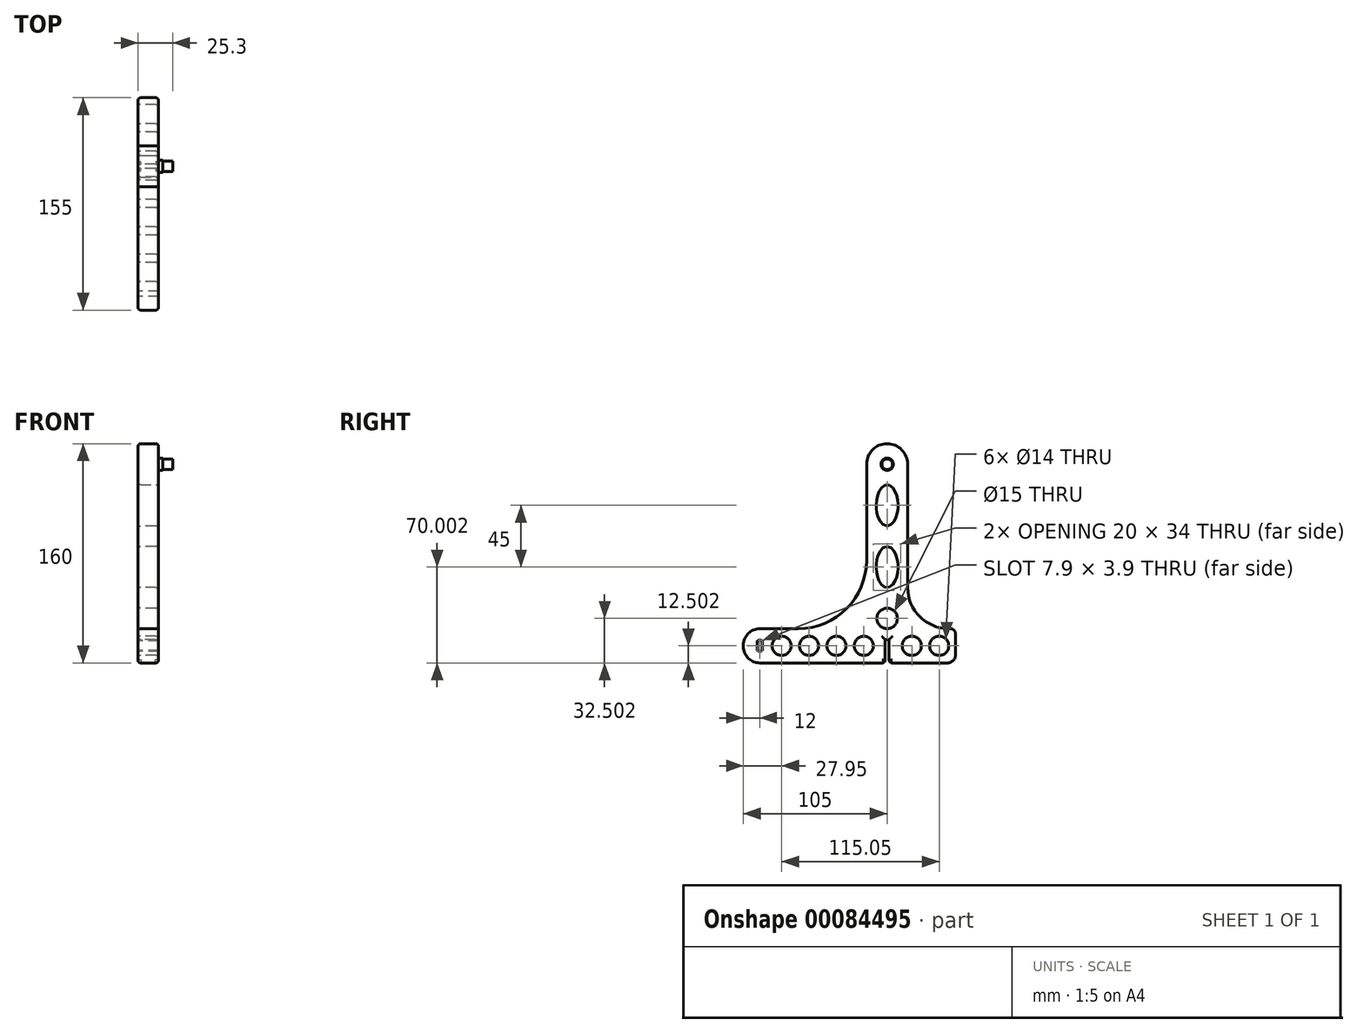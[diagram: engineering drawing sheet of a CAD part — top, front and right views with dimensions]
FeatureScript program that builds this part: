
annotation { "Feature Type Name" : "Feature", "Feature Type Description" : "" }
export const myFeature = defineFeature(function(context is Context, id is Id, definition is map)
    precondition{}
    {
        {
            var Q0;
            Q0=qCreatedBy(makeId("Right.planeOp"),FACE);
            var sketch = newSketch(context, id + "F0", { "sketchPlane" : qUnion([Q0])});
            skArc(sketch, "E0", {"start": v(15, 65.9) * mm, "mid": v(0, 80.9) * mm, "end": v(-15, 65.9) * mm});
            skLineSegment(sketch, "E1.bottom", {"start": v(-15, 65.9) * mm, "end": v(15, 65.9) * mm, "construction": true});
            skLineSegment(sketch, "E1.top", {"start": v(-15, -79.1) * mm, "end": v(-1.45, -79.1) * mm});
            skLineSegment(sketch, "E1.left", {"start": v(-15, 65.9) * mm, "end": v(-15, -4.1) * mm});
            skLineSegment(sketch, "E1.right", {"start": v(15, 65.9) * mm, "end": v(15, -24.1) * mm});
            skLineSegment(sketch, "E2.bottom", {"start": v(15, -79.1) * mm, "end": v(44, -79.1) * mm});
            skLineSegment(sketch, "E2.top", {"start": v(45, -54.1) * mm, "end": v(46, -54.1) * mm});
            skLineSegment(sketch, "E2.left", {"start": v(15, -79.1) * mm, "end": v(15, -54.1) * mm, "construction": true});
            skLineSegment(sketch, "E2.right", {"start": v(50, -73.1) * mm, "end": v(50, -58.1) * mm});
            skPoint(sketch, "E3.newPointA", {"position": v(15, -54.1) * mm});
            skPoint(sketch, "E3.newPointB", {"position": v(15, -54.1) * mm});
            skArc(sketch, "E3.filletArc", {"start": v(15, -24.1) * mm, "mid": v(23.79, -45.31) * mm, "end": v(45, -54.1) * mm});
            skPoint(sketch, "E4.visualSharp", {"position": v(50, -54.1) * mm});
            skArc(sketch, "E4.filletArc", {"start": v(50, -58.1) * mm, "mid": v(48.83, -55.27) * mm, "end": v(46, -54.1) * mm});
            skPoint(sketch, "E5.visualSharp", {"position": v(50, -79.1) * mm});
            skArc(sketch, "E5.filletArc", {"start": v(44, -79.1) * mm, "mid": v(48.24, -77.34) * mm, "end": v(50, -73.1) * mm});
            skLineSegment(sketch, "E6", {"start": v(50, -54.1) * mm, "end": v(50, -79.1) * mm, "construction": true});
            skLineSegment(sketch, "E7.bottom", {"start": v(-15, -79.1) * mm, "end": v(-93, -79.1) * mm});
            skLineSegment(sketch, "E7.top", {"start": v(-65, -54.1) * mm, "end": v(-93, -54.1) * mm});
            skLineSegment(sketch, "E7.right", {"start": v(-105, -67.1) * mm, "end": v(-105, -66.1) * mm});
            skArc(sketch, "E8.filletArc", {"start": v(-65, -54.1) * mm, "mid": v(-29.64, -39.45) * mm, "end": v(-15, -4.1) * mm});
            skPoint(sketch, "E9.visualSharp", {"position": v(-105, -54.1) * mm});
            skArc(sketch, "E9.filletArc", {"start": v(-93, -54.1) * mm, "mid": v(-101.49, -57.61) * mm, "end": v(-105, -66.1) * mm});
            skPoint(sketch, "E10.visualSharp", {"position": v(-105, -79.1) * mm});
            skArc(sketch, "E10.filletArc", {"start": v(-105, -67.1) * mm, "mid": v(-101.49, -75.58) * mm, "end": v(-93, -79.1) * mm});
            skLineSegment(sketch, "E11", {"start": v(45, -54.1) * mm, "end": v(-65, -54.1) * mm, "construction": true});
            skLineSegment(sketch, "E12", {"start": v(0, 65.9) * mm, "end": v(0, -54.1) * mm, "construction": true});
            skPoint(sketch, "E13", {"position": v(0, 5.9) * mm});
            skLineSegment(sketch, "E14", {"start": v(0, 5.9) * mm, "end": v(0, 65.9) * mm, "construction": true});
            skPoint(sketch, "E15", {"position": v(0, 35.9) * mm});
            skLineSegment(sketch, "E16", {"start": v(0, 5.9) * mm, "end": v(0, -54.1) * mm, "construction": true});
            skPoint(sketch, "E17", {"position": v(0, -24.1) * mm});
            skLineSegment(sketch, "E18", {"start": v(50, -66.6) * mm, "end": v(-105, -66.6) * mm, "construction": true});
            skLineSegment(sketch, "E19", {"start": v(0, 65.9) * mm, "end": v(0, 35.9) * mm, "construction": true});
            skLineSegment(sketch, "E20", {"start": v(0, 35.9) * mm, "end": v(0, 5.9) * mm, "construction": true});
            skLineSegment(sketch, "E21", {"start": v(0, 5.9) * mm, "end": v(0, -24.1) * mm, "construction": true});
            skLineSegment(sketch, "E22", {"start": v(0, -24.1) * mm, "end": v(0, -54.1) * mm, "construction": true});
            skPoint(sketch, "E23", {"position": v(0, 50.9) * mm});
            skPoint(sketch, "E24", {"position": v(0, 20.9) * mm});
            skPoint(sketch, "E25", {"position": v(0, -9.1) * mm});
            skPoint(sketch, "E26", {"position": v(0, -39.1) * mm});
            skEllipse(sketch, "E27", {"center": v(0, 35.9) * mm, "majorRadius": 15 * mm, "minorRadius": 8 * mm, "majorAxis": v(0, -1)});
            skLineSegment(sketch, "E28", {"start": v(8, 65.9) * mm, "end": v(8, -54.1) * mm, "construction": true});
            skEllipse(sketch, "E29", {"center": v(0, -9.1) * mm, "majorRadius": 15 * mm, "minorRadius": 8 * mm, "majorAxis": v(0, 1)});
            skPoint(sketch, "E30", {"position": v(0, -46.6) * mm});
            skCircle(sketch, "E31", {"center": v(0, -46.6) * mm, "radius": 7.5 * mm});
            skPoint(sketch, "E32", {"position": v(-93, -66.6) * mm});
            skLineSegment(sketch, "E33.bottom", {"start": v(1.45, -62.1) * mm, "end": v(-1.45, -62.1) * mm});
            skLineSegment(sketch, "E33.left", {"start": v(1.45, -62.1) * mm, "end": v(1.45, -79.1) * mm});
            skLineSegment(sketch, "E33.right", {"start": v(-1.45, -62.1) * mm, "end": v(-1.45, -79.1) * mm});
            skPoint(sketch, "E33.middle", {"position": v(0, -79.1) * mm});
            skPoint(sketch, "E33.top.end.orphan", {"position": v(-1.45, -96.1) * mm});
            skPoint(sketch, "E33.top.start.orphan", {"position": v(1.45, -96.1) * mm});
            skLineSegment(sketch, "E34.trimOffspring", {"start": v(1.45, -79.1) * mm, "end": v(15, -79.1) * mm});
            skCircle(sketch, "E35", {"center": v(0, 65.9) * mm, "radius": 4.5 * mm});
            skCircle(sketch, "E36", {"center": v(0, 65.9) * mm, "radius": 3.9 * mm});
            skCircle(sketch, "E37", {"center": v(-93, -66.6) * mm, "radius": 3.95 * mm});
            skLineSegment(sketch, "E38", {"start": v(-89.05, -54.1) * mm, "end": v(-89.05, -79.1) * mm, "construction": true});
            skLineSegment(sketch, "E39", {"start": v(-96.95, -54.77) * mm, "end": v(-96.95, -78.43) * mm, "construction": true});
            skLineSegment(sketch, "E40", {"start": v(-91.05, -63.16) * mm, "end": v(-91.05, -70.03) * mm});
            skLineSegment(sketch, "E41", {"start": v(-94.95, -63.16) * mm, "end": v(-94.95, -70.03) * mm});
            skLineSegment(sketch, "E42", {"start": v(-96.95, -66.6) * mm, "end": v(-94.95, -66.6) * mm, "construction": true});
            skPoint(sketch, "E43.orphan", {"position": v(-94.95, -54.26) * mm});
            skPoint(sketch, "E44.orphan", {"position": v(-94.95, -78.94) * mm});
            skLineSegment(sketch, "E45", {"start": v(-91.05, -66.6) * mm, "end": v(-89.05, -66.6) * mm, "construction": true});
            skLineSegment(sketch, "E46", {"start": v(-94.95, -66.6) * mm, "end": v(-96.95, -66.6) * mm, "construction": true});
            skCircle(sketch, "E47", {"center": v(-77.05, -66.6) * mm, "radius": 7 * mm});
            skCircle(sketch, "E48.1.0.0", {"center": v(-57.05, -66.6) * mm, "radius": 7 * mm});
            skCircle(sketch, "E48.2.0.0", {"center": v(-37.05, -66.6) * mm, "radius": 7 * mm});
            skLineSegment(sketch, "E48.direction1", {"start": v(-77.05, -66.6) * mm, "end": v(-57.05, -66.6) * mm, "construction": true});
            skCircle(sketch, "E49", {"center": v(38, -66.6) * mm, "radius": 7 * mm});
            skCircle(sketch, "E50.1.0.0", {"center": v(18, -66.6) * mm, "radius": 7 * mm});
            skLineSegment(sketch, "E50.1.0.1", {"start": v(-5, -79.1) * mm, "end": v(24, -79.1) * mm});
            skLineSegment(sketch, "E50.direction1", {"start": v(38, -66.6) * mm, "end": v(18, -66.6) * mm, "construction": true});
            skCircle(sketch, "E51.0.3.0", {"center": v(-17.05, -66.6) * mm, "radius": 7 * mm});
            skSolve(sketch);
        }
        {
            var Q0;
            Q0=makeQuery(id+"F0.imprint","IMPRINT",FACE,{"disambiguationData":[TD([[makeQuery(id+"F0.imprint","IMPRINT",EDGE,{"derivedFrom":sQuery(id+"F0.wireOp",EDGE,"E0")}),1.0]])]});
            var Q1;
            {var subQ0=sQuery(id+"F0.wireOp",EDGE,"E40");Q1=makeQuery(id+"F0.imprint","IMPRINT",FACE,{"disambiguationData":[TD([[makeQuery(id+"F0.imprint","IMPRINT",EDGE,{"derivedFrom":subQ0}),1.0]])]});}
            var Q2;
            {var subQ0=sQuery(id+"F0.wireOp",EDGE,"E41");Q2=makeQuery(id+"F0.imprint","IMPRINT",FACE,{"disambiguationData":[TD([[makeQuery(id+"F0.imprint","IMPRINT",EDGE,{"derivedFrom":subQ0}),-1.0]])]});}
            extrude(context, id + "F1", {"entities" : qUnion([Q0, Q1, Q2]), "depth" : 15 * mm});
        }
        {
            var Q0;
            Q0=makeQuery(id+"F0.imprint","IMPRINT",FACE,{"disambiguationData":[TD([[makeQuery(id+"F0.imprint","IMPRINT",EDGE,{"derivedFrom":sQuery(id+"F0.wireOp",EDGE,"E35")}),1.0]])]});
            extrude(context, id + "F2", {"entities" : qUnion([Q0]), "operationType" : NewBodyOperationType.ADD, "depth" : 18 * mm});
        }
        {
            var Q0;
            Q0=makeQuery(id+"F0.imprint","IMPRINT",FACE,{"disambiguationData":[TD([[makeQuery(id+"F0.imprint","IMPRINT",EDGE,{"derivedFrom":sQuery(id+"F0.wireOp",EDGE,"E36")}),1.0]])]});
            extrude(context, id + "F3", {"entities" : qUnion([Q0]), "operationType" : NewBodyOperationType.ADD, "depth" : 25.3 * mm});
        }
        {
            var Q0;
            Q0=makeQuery(id+"F1.opExtrude","CAP_EDGE",EDGE,{"disambiguationData":[OSD([sQuery(id+"F0.wireOp",EDGE,"E1.right")])],"isStart":false});
            var Q1;
            Q1=makeQuery(id+"F1.opExtrude","CAP_EDGE",EDGE,{"disambiguationData":[OSD([sQuery(id+"F0.wireOp",EDGE,"E1.right")])],"isStart":true});
            var Q2;
            Q2=makeQuery(id+"F1.opExtrude","CAP_EDGE",EDGE,{"disambiguationData":[OSD([sQuery(id+"F0.wireOp",EDGE,"E27")])],"isStart":false});
            var Q3;
            Q3=makeQuery(id+"F1.opExtrude","CAP_EDGE",EDGE,{"disambiguationData":[OSD([sQuery(id+"F0.wireOp",EDGE,"E27")])],"isStart":true});
            var Q4;
            Q4=makeQuery(id+"F1.opExtrude","CAP_EDGE",EDGE,{"disambiguationData":[OSD([sQuery(id+"F0.wireOp",EDGE,"E29")])],"isStart":true});
            var Q5;
            Q5=makeQuery(id+"F1.opExtrude","CAP_EDGE",EDGE,{"disambiguationData":[OSD([sQuery(id+"F0.wireOp",EDGE,"E29")])],"isStart":false});
            var Q6;
            Q6=makeQuery(id+"F1.opExtrude","CAP_EDGE",EDGE,{"disambiguationData":[OSD([sQuery(id+"F0.wireOp",EDGE,"E31")])],"isStart":true});
            var Q7;
            Q7=makeQuery(id+"F1.opExtrude","CAP_EDGE",EDGE,{"disambiguationData":[OSD([sQuery(id+"F0.wireOp",EDGE,"E31")])],"isStart":false});
            var Q8;
            Q8=makeQuery(id+"F1.opExtrude","CAP_EDGE",EDGE,{"disambiguationData":[OSD([sQuery(id+"F0.wireOp",EDGE,"E35")])],"isStart":false});
            var Q9;
            Q9=makeQuery(id+"F1.opExtrude","CAP_EDGE",EDGE,{"disambiguationData":[OSD([sQuery(id+"F0.wireOp",EDGE,"E47")])],"isStart":false});
            var Q10;
            Q10=makeQuery(id+"F1.opExtrude","CAP_EDGE",EDGE,{"disambiguationData":[OSD([sQuery(id+"F0.wireOp",EDGE,"E48.1.0.0")])],"isStart":false});
            var Q11;
            Q11=makeQuery(id+"F1.opExtrude","CAP_EDGE",EDGE,{"disambiguationData":[OSD([sQuery(id+"F0.wireOp",EDGE,"E48.2.0.0")])],"isStart":false});
            var Q12;
            Q12=makeQuery(id+"F1.opExtrude","CAP_EDGE",EDGE,{"disambiguationData":[OSD([sQuery(id+"F0.wireOp",EDGE,"E48.2.0.0")])],"isStart":true});
            var Q13;
            Q13=makeQuery(id+"F1.opExtrude","CAP_EDGE",EDGE,{"disambiguationData":[OSD([sQuery(id+"F0.wireOp",EDGE,"E48.1.0.0")])],"isStart":true});
            var Q14;
            Q14=makeQuery(id+"F1.opExtrude","CAP_EDGE",EDGE,{"disambiguationData":[OSD([sQuery(id+"F0.wireOp",EDGE,"E47")])],"isStart":true});
            var Q15;
            Q15=makeQuery(id+"F1.opExtrude","CAP_EDGE",EDGE,{"disambiguationData":[OSD([sQuery(id+"F0.wireOp",EDGE,"E51.0.3.0")])],"isStart":false});
            var Q16;
            Q16=makeQuery(id+"F1.opExtrude","CAP_EDGE",EDGE,{"disambiguationData":[OSD([sQuery(id+"F0.wireOp",EDGE,"E50.1.0.0")])],"isStart":false});
            var Q17;
            Q17=makeQuery(id+"F1.opExtrude","CAP_EDGE",EDGE,{"disambiguationData":[OSD([sQuery(id+"F0.wireOp",EDGE,"E49")])],"isStart":false});
            var Q18;
            Q18=makeQuery(id+"F1.opExtrude","CAP_EDGE",EDGE,{"disambiguationData":[OSD([sQuery(id+"F0.wireOp",EDGE,"E51.0.3.0")])],"isStart":true});
            var Q19;
            Q19=makeQuery(id+"F1.opExtrude","CAP_EDGE",EDGE,{"disambiguationData":[OSD([sQuery(id+"F0.wireOp",EDGE,"E50.1.0.0")])],"isStart":true});
            var Q20;
            Q20=makeQuery(id+"F1.opExtrude","CAP_EDGE",EDGE,{"disambiguationData":[OSD([sQuery(id+"F0.wireOp",EDGE,"E49")])],"isStart":true});
            fillet(context, id + "F4", {"entities" : qUnion([Q0, Q1, Q2, Q3, Q4, Q5, Q6, Q7, Q8, Q9, Q10, Q11, Q12, Q13, Q14, Q15, Q16, Q17, Q18, Q19, Q20]), "radius" : 2 * mm, "tangentPropagation" : true, "allowEdgeOverflow" : false});
        }
        {
            var Q0;
            Q0=makeQuery(id+"F1.opExtrude","CAP_EDGE",EDGE,{"disambiguationData":[OSD([sQuery(id+"F0.wireOp",EDGE,"E33.right")])],"isStart":false});
            var Q1;
            Q1=makeQuery(id+"F1.opExtrude","CAP_EDGE",EDGE,{"disambiguationData":[OSD([sQuery(id+"F0.wireOp",EDGE,"E33.left")])],"isStart":false});
            var Q2;
            Q2=makeQuery(id+"F1.opExtrude","CAP_EDGE",EDGE,{"disambiguationData":[OSD([sQuery(id+"F0.wireOp",EDGE,"E33.bottom")])],"isStart":false});
            var Q3;
            Q3=makeQuery(id+"F1.opExtrude","CAP_EDGE",EDGE,{"disambiguationData":[OSD([sQuery(id+"F0.wireOp",EDGE,"E33.bottom")])],"isStart":true});
            fillet(context, id + "F5", {"entities" : qUnion([Q0, Q1, Q2, Q3]), "radius" : 2.3 * mm, "tangentPropagation" : true, "allowEdgeOverflow" : false});
        }
    });
